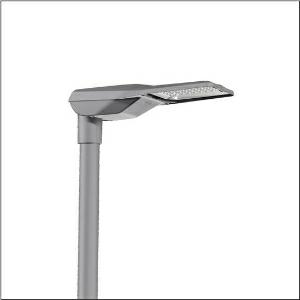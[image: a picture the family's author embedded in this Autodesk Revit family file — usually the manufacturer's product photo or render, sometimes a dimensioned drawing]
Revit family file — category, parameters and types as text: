
# Revit family: streetlight_sl_21_iq_mini___pl52_5xe2h31d08gb_8f57
name_source: partatom
category: Lighting Fixtures
units: mm (PartAtom-declared; Revit-internal decimal feet)

## family parameters
Cut with Voids When Loaded = No
Host = Face
Light Source = No
Part Type = Normal
Room Calculation Point = No
Round Connector Dimension = Use Diameter
Shared = No

## types (1)
- --- (1 x LED, 5580 lm, 37.1 W, 3000K)
    Apparent Load = 37 VA
    CIE Flux Codes = 27 59 98 100 100
    Color Rendering = 70
    Color Temperature = 3000K
    Default Elevation = 1800 mm
    Description = Streetlight SL 21 iQ mini, mast luminaire, primary light control with lens, of PMMA, primary optical cover: cover, of toughened safety glass, transparent, light distribution: PL52, light emission: direct distribution, primary light characteristic: asymmetric, installation type: post-top, side-entry, LED, High Power LED, rated luminous flux: 5.580lm, luminous efficacy: 150lm/W, light colour: 730, colour temperature: 3000K, control gear: iQ-Comfort, control: Auto-Match, Temp-Guard, Lumen-Switch, Night-Set, Smart-Wire, Light-Fading, Desk-Remote (wireless, voltage-free reading and setting of iQ features in the workshop via application-optimized NFC function/RFID function), optimised constant luminous flux control (CLO 2.0), pre-setting: linear dimming characteristic, mains connection: 220..240V, AC, 50/60Hz, start of lifetime: 37W, end of service life: 39W, reduction: 18W, luminaire housing, of diecast aluminium, powder-coated, Siteco® metallic grey (DB 702S), corrosivity category C5 mid according to DIN EN ISO 12944, please order mast flange separately, inclination adjustable: 0°, 5°, 10°, 15°, sealing non-destructively replaceable, multi-level sealing system, length: 628mm, width: 235mm, height: 110mm, mast flange for spigot size: 42mm (side-entry): 5XC10008XM4, 60/48mm (side-entry/post-top): 5XC10108XM2, 76/60mm (side-entry/post-top): 5XC10108XM1, mounting height: 4..8m, protection rating (complete): IP66, insulation class (complete): insulation class II (safety insulation), certification: CE, ENEC, ENEC+, VDE, impact resistance: IK10, permissible operating ambient temperature for outdoor applications: -40..+50°C, standard-compliant lighting for roads and squares, packaging unit: 1 piece

Light Distribution: PL52
    Height = 110 mm
    Lamp = 1 x LED
    Lamp Light Flux = 5580 lm
    Lamp Power = 37.1 W
    Lamp count = 1
    Length = 625 mm
    Luminous efficacy = 150 lm/W
    Manufacturer = Siteco
    ModVariant = No
    Model = 5XE2H31D08GB
    Number of Poles = 1
    OnlyDefault = Yes
    Power Factor = 1
    Product Name = Streetlight SL 21 iQ mini | PL52
    Product group = mast luminaire | pylon top
    ProductGroupID = 6100
    Protection Class = Protection class II
    Protection Degree = IP 66
    RLX_Detail_Level = 1
    RLX_Emergency_Light_Flux = 0 lm
    RLX_Emergency_Type = 0
    RLX_Emergency_Type_DB = No
    RlxData = <blob elided: 35897 chars, md5=34e8f862>
    Socket = socket
    Standby Power = 0 W
    System Light Flux = 5580 lm
    System Power = 37 W
    Type Comments = factory setting: luminous flux: 100 % | dim-lin: 254 | 385 mA
    Type Image = l_1003519.jpg
    URL = http://relux.com
    VarID = @adj_190356
    Voltage = 0 V
    Weight = 0.00 kg
    Width = 234 mm

## geometry (parser evidence)
native form markers: Blend x4, Sweep x10
no freeform markers — native parametric forms only
